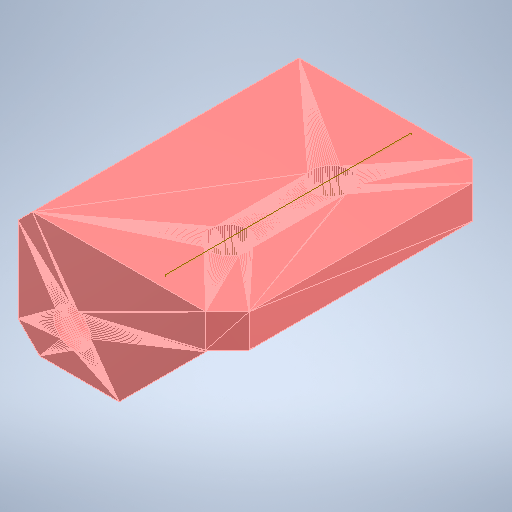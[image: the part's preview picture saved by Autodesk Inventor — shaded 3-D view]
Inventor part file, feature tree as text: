
AUTODESK INVENTOR PART (.ipt)
format: ipt  version: 2025.2 (Build 292293000, 293)  size: 262,656 bytes
history: native  units: in
note: dims shown in document units (in); Inventor stores cm internally (conversion verified against a paired STEP export)
features: other x2, plane x1
ambient origin geometry x8: Origin, YZ Plane, XZ Plane, XY Plane, X Axis, Y Axis, Z Axis, Center Point
feature tree (3):
  other  "1 X Right_Idler_Mount"
  plane  "Work Plane1"
  other  "MeshFeature1"
